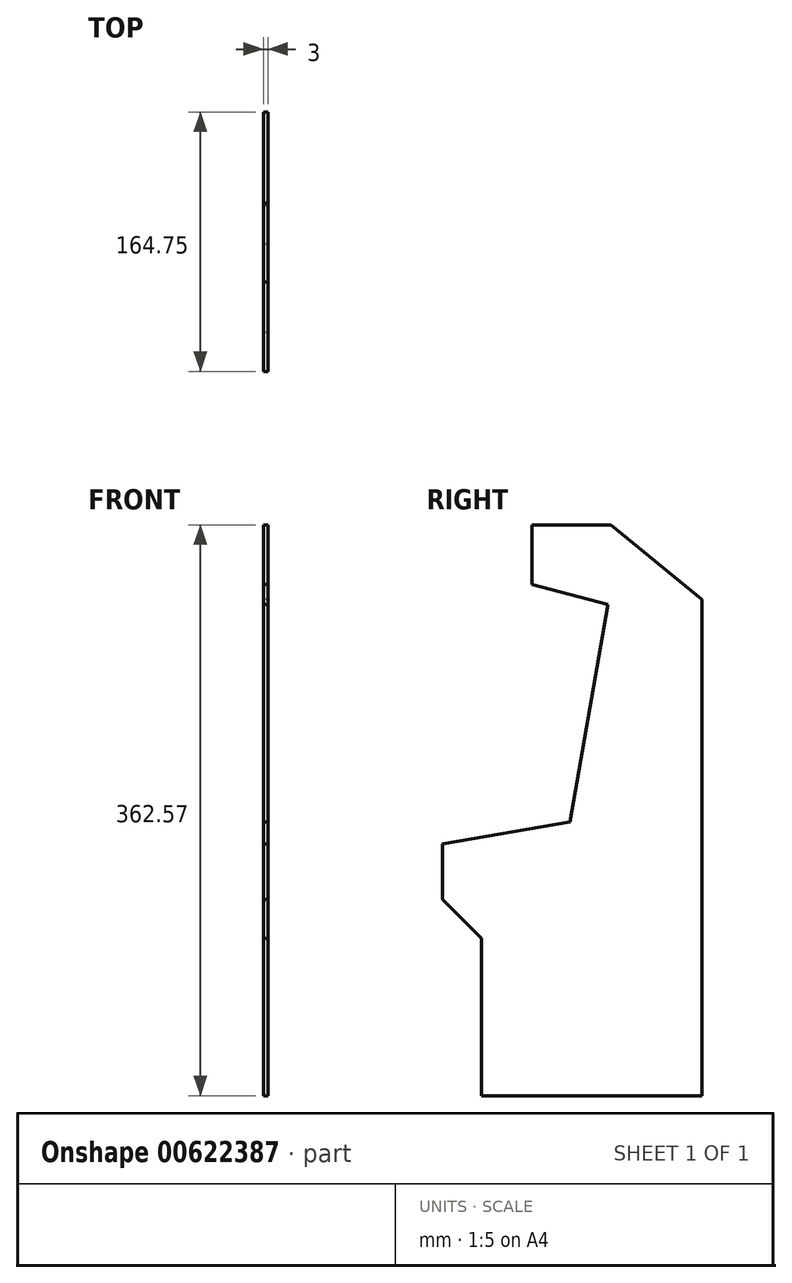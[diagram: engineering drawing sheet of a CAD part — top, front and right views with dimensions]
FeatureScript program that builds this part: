
annotation { "Feature Type Name" : "Feature", "Feature Type Description" : "" }
export const myFeature = defineFeature(function(context is Context, id is Id, definition is map)
    precondition{}
    {
        {
            var Q0;
            Q0=qCreatedBy(makeId("Right.planeOp"),FACE);
            var sketch = newSketch(context, id + "F0", { "sketchPlane" : qUnion([Q0])});
            skLineSegment(sketch, "E0.MirrorCS", {"start": v(140, 315) * mm, "end": v(140, 0) * mm});
            skLineSegment(sketch, "E1.MirrorCS", {"start": v(82.02, 362.57) * mm, "end": v(140, 315) * mm});
            skLineSegment(sketch, "E2.MirrorCS", {"start": v(32.02, 362.57) * mm, "end": v(82.02, 362.57) * mm});
            skLineSegment(sketch, "E3.MirrorCS", {"start": v(32.02, 324.8) * mm, "end": v(32.02, 362.57) * mm});
            skLineSegment(sketch, "E4.MirrorCS", {"start": v(80.32, 311.86) * mm, "end": v(32.02, 324.8) * mm});
            skLineSegment(sketch, "E5.MirrorCS", {"start": v(56, 173.99) * mm, "end": v(80.32, 311.86) * mm});
            skLineSegment(sketch, "E6.MirrorCS", {"start": v(-24.75, 159.75) * mm, "end": v(56, 173.99) * mm});
            skLineSegment(sketch, "E7.MirrorCS", {"start": v(-24.75, 124.75) * mm, "end": v(-24.75, 159.75) * mm});
            skLineSegment(sketch, "E8.MirrorCS", {"start": v(0, 100) * mm, "end": v(-24.75, 124.75) * mm});
            skLineSegment(sketch, "E9.MirrorCS", {"start": v(0, 0) * mm, "end": v(0, 100) * mm});
            skLineSegment(sketch, "E10.MirrorCS", {"start": v(140, 0) * mm, "end": v(0, 0) * mm});
            skSolve(sketch);
        }
        {
            var Q0;
            Q0 = qSketchRegion(id + "F0", true);
            extrude(context, id + "F1", {"entities" : qUnion([Q0]), "depth" : 3 * mm, "offsetDistance" : 25 * mm});
        }
    });
